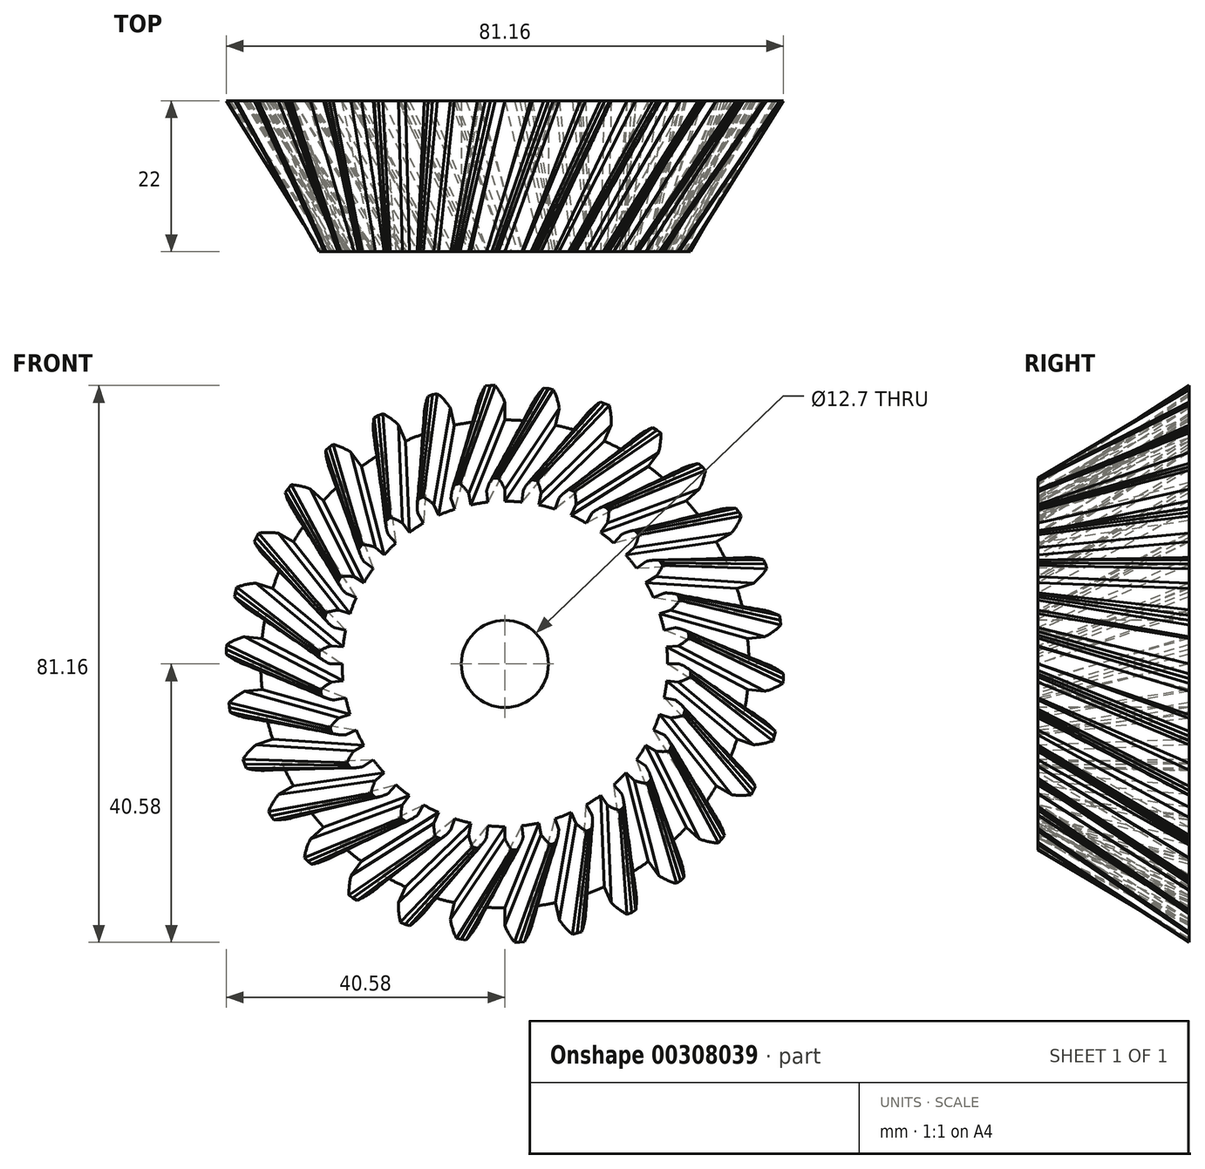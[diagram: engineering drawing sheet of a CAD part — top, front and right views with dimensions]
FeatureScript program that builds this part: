
annotation { "Feature Type Name" : "Feature", "Feature Type Description" : "" }
export const myFeature = defineFeature(function(context is Context, id is Id, definition is map)
    precondition{}
    {
        {
            var Q0;
            Q0=qCreatedBy(makeId("Front.planeOp"),FACE);
            var sketch = newSketch(context, id + "F0", { "sketchPlane" : qUnion([Q0])});
            skArc(sketch, "E0", {"start": v(-3.72, 35.37) * mm, "mid": v(-5.56, 35.12) * mm, "end": v(-7.4, 34.78) * mm});
            skLineSegment(sketch, "E1", {"start": v(0, 38.1) * mm, "end": v(0, 35.56) * mm});
            skLineSegment(sketch, "E2", {"start": v(-1.42, 40.58) * mm, "end": v(-2.13, 40.58) * mm});
            skArc(sketch, "E3.trimOffspring", {"start": v(0, 38.1) * mm, "mid": v(-0.63, 39.41) * mm, "end": v(-1.45, 40.61) * mm});
            skLineSegment(sketch, "E4.MirrorCS", {"start": v(-2.83, 40.5) * mm, "end": v(-2.13, 40.58) * mm});
            skArc(sketch, "E5.MirrorCS", {"start": v(-3.98, 37.9) * mm, "mid": v(-3.5, 39.26) * mm, "end": v(-2.8, 40.54) * mm});
            skLineSegment(sketch, "E6.MirrorCS", {"start": v(-3.98, 37.9) * mm, "end": v(-3.72, 35.37) * mm});
            skLineSegment(sketch, "E7.1.0", {"start": v(-11.77, 36.24) * mm, "end": v(-10.99, 33.82) * mm});
            skArc(sketch, "E7.1.1", {"start": v(-11.77, 36.24) * mm, "mid": v(-11.58, 37.68) * mm, "end": v(-11.18, 39.07) * mm});
            skLineSegment(sketch, "E7.1.2", {"start": v(-11.2, 39.04) * mm, "end": v(-10.52, 39.25) * mm});
            skLineSegment(sketch, "E7.1.3", {"start": v(-9.83, 39.4) * mm, "end": v(-10.52, 39.25) * mm});
            skArc(sketch, "E7.1.4", {"start": v(-7.92, 37.27) * mm, "mid": v(-8.8, 38.42) * mm, "end": v(-9.86, 39.43) * mm});
            skLineSegment(sketch, "E7.1.5", {"start": v(-7.92, 37.27) * mm, "end": v(-7.4, 34.78) * mm});
            skLineSegment(sketch, "E7.2.0", {"start": v(-19.05, 33) * mm, "end": v(-17.78, 30.8) * mm});
            skArc(sketch, "E7.2.1", {"start": v(-19.05, 33) * mm, "mid": v(-19.16, 34.45) * mm, "end": v(-19.06, 35.9) * mm});
            skLineSegment(sketch, "E7.2.2", {"start": v(-19.06, 35.86) * mm, "end": v(-18.45, 36.2) * mm});
            skLineSegment(sketch, "E7.2.3", {"start": v(-17.8, 36.5) * mm, "end": v(-18.45, 36.2) * mm});
            skArc(sketch, "E7.2.4", {"start": v(-15.5, 34.8) * mm, "mid": v(-16.6, 35.75) * mm, "end": v(-17.84, 36.52) * mm});
            skLineSegment(sketch, "E7.2.5", {"start": v(-15.5, 34.8) * mm, "end": v(-14.46, 32.49) * mm});
            skLineSegment(sketch, "E7.3.0", {"start": v(-25.5, 28.31) * mm, "end": v(-23.8, 26.43) * mm});
            skArc(sketch, "E7.3.1", {"start": v(-25.5, 28.31) * mm, "mid": v(-25.9, 29.7) * mm, "end": v(-26.1, 31.15) * mm});
            skLineSegment(sketch, "E7.3.2", {"start": v(-26.1, 31.1) * mm, "end": v(-25.57, 31.58) * mm});
            skLineSegment(sketch, "E7.3.3", {"start": v(-25, 32) * mm, "end": v(-25.57, 31.58) * mm});
            skArc(sketch, "E7.3.4", {"start": v(-22.4, 30.82) * mm, "mid": v(-23.67, 31.52) * mm, "end": v(-25.04, 32) * mm});
            skLineSegment(sketch, "E7.3.5", {"start": v(-22.4, 30.82) * mm, "end": v(-20.9, 28.77) * mm});
            skLineSegment(sketch, "E7.4.0", {"start": v(-30.82, 22.4) * mm, "end": v(-28.77, 20.9) * mm});
            skArc(sketch, "E7.4.1", {"start": v(-30.82, 22.4) * mm, "mid": v(-31.52, 23.67) * mm, "end": v(-32, 25.04) * mm});
            skLineSegment(sketch, "E7.4.2", {"start": v(-32, 25) * mm, "end": v(-31.58, 25.57) * mm});
            skLineSegment(sketch, "E7.4.3", {"start": v(-31.1, 26.1) * mm, "end": v(-31.58, 25.57) * mm});
            skArc(sketch, "E7.4.4", {"start": v(-28.31, 25.5) * mm, "mid": v(-29.7, 25.9) * mm, "end": v(-31.15, 26.1) * mm});
            skLineSegment(sketch, "E7.4.5", {"start": v(-28.31, 25.5) * mm, "end": v(-26.43, 23.8) * mm});
            skLineSegment(sketch, "E7.5.0", {"start": v(-34.8, 15.5) * mm, "end": v(-32.49, 14.46) * mm});
            skArc(sketch, "E7.5.1", {"start": v(-34.8, 15.5) * mm, "mid": v(-35.75, 16.6) * mm, "end": v(-36.52, 17.84) * mm});
            skLineSegment(sketch, "E7.5.2", {"start": v(-36.5, 17.8) * mm, "end": v(-36.2, 18.45) * mm});
            skLineSegment(sketch, "E7.5.3", {"start": v(-35.86, 19.06) * mm, "end": v(-36.2, 18.45) * mm});
            skArc(sketch, "E7.5.4", {"start": v(-33, 19.05) * mm, "mid": v(-34.45, 19.16) * mm, "end": v(-35.9, 19.06) * mm});
            skLineSegment(sketch, "E7.5.5", {"start": v(-33, 19.05) * mm, "end": v(-30.8, 17.78) * mm});
            skLineSegment(sketch, "E7.6.0", {"start": v(-37.27, 7.92) * mm, "end": v(-34.78, 7.4) * mm});
            skArc(sketch, "E7.6.1", {"start": v(-37.27, 7.92) * mm, "mid": v(-38.42, 8.8) * mm, "end": v(-39.43, 9.86) * mm});
            skLineSegment(sketch, "E7.6.2", {"start": v(-39.4, 9.83) * mm, "end": v(-39.25, 10.52) * mm});
            skLineSegment(sketch, "E7.6.3", {"start": v(-39.04, 11.2) * mm, "end": v(-39.25, 10.52) * mm});
            skArc(sketch, "E7.6.4", {"start": v(-36.24, 11.77) * mm, "mid": v(-37.68, 11.58) * mm, "end": v(-39.07, 11.18) * mm});
            skLineSegment(sketch, "E7.6.5", {"start": v(-36.24, 11.77) * mm, "end": v(-33.82, 10.99) * mm});
            skLineSegment(sketch, "E7.7.0", {"start": v(-38.1, 0) * mm, "end": v(-35.56, 0) * mm});
            skArc(sketch, "E7.7.1", {"start": v(-38.1, 0) * mm, "mid": v(-39.41, 0.63) * mm, "end": v(-40.61, 1.45) * mm});
            skLineSegment(sketch, "E7.7.2", {"start": v(-40.58, 1.42) * mm, "end": v(-40.58, 2.13) * mm});
            skLineSegment(sketch, "E7.7.3", {"start": v(-40.5, 2.83) * mm, "end": v(-40.58, 2.13) * mm});
            skArc(sketch, "E7.7.4", {"start": v(-37.9, 3.98) * mm, "mid": v(-39.26, 3.5) * mm, "end": v(-40.54, 2.8) * mm});
            skLineSegment(sketch, "E7.7.5", {"start": v(-37.9, 3.98) * mm, "end": v(-35.37, 3.72) * mm});
            skLineSegment(sketch, "E7.8.0", {"start": v(-37.27, -7.92) * mm, "end": v(-34.78, -7.4) * mm});
            skArc(sketch, "E7.8.1", {"start": v(-37.27, -7.92) * mm, "mid": v(-38.68, -7.58) * mm, "end": v(-40.03, -7.03) * mm});
            skLineSegment(sketch, "E7.8.2", {"start": v(-40, -7.05) * mm, "end": v(-40.14, -6.36) * mm});
            skLineSegment(sketch, "E7.8.3", {"start": v(-40.21, -5.65) * mm, "end": v(-40.14, -6.36) * mm});
            skArc(sketch, "E7.8.4", {"start": v(-37.9, -3.98) * mm, "mid": v(-39.13, -4.74) * mm, "end": v(-40.24, -5.68) * mm});
            skLineSegment(sketch, "E7.8.5", {"start": v(-37.9, -3.98) * mm, "end": v(-35.37, -3.72) * mm});
            skLineSegment(sketch, "E7.9.0", {"start": v(-34.8, -15.5) * mm, "end": v(-32.49, -14.46) * mm});
            skArc(sketch, "E7.9.1", {"start": v(-34.8, -15.5) * mm, "mid": v(-36.26, -15.46) * mm, "end": v(-37.7, -15.2) * mm});
            skLineSegment(sketch, "E7.9.2", {"start": v(-37.65, -15.2) * mm, "end": v(-37.94, -14.56) * mm});
            skLineSegment(sketch, "E7.9.3", {"start": v(-38.16, -13.9) * mm, "end": v(-37.94, -14.56) * mm});
            skArc(sketch, "E7.9.4", {"start": v(-36.24, -11.77) * mm, "mid": v(-37.29, -12.77) * mm, "end": v(-38.18, -13.92) * mm});
            skLineSegment(sketch, "E7.9.5", {"start": v(-36.24, -11.77) * mm, "end": v(-33.82, -10.99) * mm});
            skLineSegment(sketch, "E7.10.0", {"start": v(-30.82, -22.4) * mm, "end": v(-28.77, -20.9) * mm});
            skArc(sketch, "E7.10.1", {"start": v(-30.82, -22.4) * mm, "mid": v(-32.25, -22.66) * mm, "end": v(-33.7, -22.7) * mm});
            skLineSegment(sketch, "E7.10.2", {"start": v(-33.67, -22.7) * mm, "end": v(-34.08, -22.13) * mm});
            skLineSegment(sketch, "E7.10.3", {"start": v(-34.44, -21.52) * mm, "end": v(-34.08, -22.13) * mm});
            skArc(sketch, "E7.10.4", {"start": v(-33, -19.05) * mm, "mid": v(-33.82, -20.25) * mm, "end": v(-34.45, -21.56) * mm});
            skLineSegment(sketch, "E7.10.5", {"start": v(-33, -19.05) * mm, "end": v(-30.8, -17.78) * mm});
            skLineSegment(sketch, "E7.11.0", {"start": v(-25.5, -28.31) * mm, "end": v(-23.8, -26.43) * mm});
            skArc(sketch, "E7.11.1", {"start": v(-25.5, -28.31) * mm, "mid": v(-26.84, -28.87) * mm, "end": v(-28.25, -29.22) * mm});
            skLineSegment(sketch, "E7.11.2", {"start": v(-28.21, -29.2) * mm, "end": v(-28.74, -28.74) * mm});
            skLineSegment(sketch, "E7.11.3", {"start": v(-29.2, -28.21) * mm, "end": v(-28.74, -28.74) * mm});
            skArc(sketch, "E7.11.4", {"start": v(-28.31, -25.5) * mm, "mid": v(-28.87, -26.84) * mm, "end": v(-29.22, -28.25) * mm});
            skLineSegment(sketch, "E7.11.5", {"start": v(-28.31, -25.5) * mm, "end": v(-26.43, -23.8) * mm});
            skLineSegment(sketch, "E7.12.0", {"start": v(-19.05, -33) * mm, "end": v(-17.78, -30.8) * mm});
            skArc(sketch, "E7.12.1", {"start": v(-19.05, -33) * mm, "mid": v(-20.25, -33.82) * mm, "end": v(-21.56, -34.45) * mm});
            skLineSegment(sketch, "E7.12.2", {"start": v(-21.52, -34.44) * mm, "end": v(-22.13, -34.08) * mm});
            skLineSegment(sketch, "E7.12.3", {"start": v(-22.7, -33.67) * mm, "end": v(-22.13, -34.08) * mm});
            skArc(sketch, "E7.12.4", {"start": v(-22.4, -30.82) * mm, "mid": v(-22.66, -32.25) * mm, "end": v(-22.7, -33.7) * mm});
            skLineSegment(sketch, "E7.12.5", {"start": v(-22.4, -30.82) * mm, "end": v(-20.9, -28.77) * mm});
            skLineSegment(sketch, "E7.13.0", {"start": v(-11.77, -36.24) * mm, "end": v(-10.99, -33.82) * mm});
            skArc(sketch, "E7.13.1", {"start": v(-11.77, -36.24) * mm, "mid": v(-12.77, -37.29) * mm, "end": v(-13.92, -38.18) * mm});
            skLineSegment(sketch, "E7.13.2", {"start": v(-13.9, -38.16) * mm, "end": v(-14.56, -37.94) * mm});
            skLineSegment(sketch, "E7.13.3", {"start": v(-15.2, -37.65) * mm, "end": v(-14.56, -37.94) * mm});
            skArc(sketch, "E7.13.4", {"start": v(-15.5, -34.8) * mm, "mid": v(-15.46, -36.26) * mm, "end": v(-15.2, -37.7) * mm});
            skLineSegment(sketch, "E7.13.5", {"start": v(-15.5, -34.8) * mm, "end": v(-14.46, -32.49) * mm});
            skLineSegment(sketch, "E7.14.0", {"start": v(-3.98, -37.9) * mm, "end": v(-3.72, -35.37) * mm});
            skArc(sketch, "E7.14.1", {"start": v(-3.98, -37.9) * mm, "mid": v(-4.74, -39.13) * mm, "end": v(-5.68, -40.24) * mm});
            skLineSegment(sketch, "E7.14.2", {"start": v(-5.65, -40.21) * mm, "end": v(-6.36, -40.14) * mm});
            skLineSegment(sketch, "E7.14.3", {"start": v(-7.05, -40) * mm, "end": v(-6.36, -40.14) * mm});
            skArc(sketch, "E7.14.4", {"start": v(-7.92, -37.27) * mm, "mid": v(-7.58, -38.68) * mm, "end": v(-7.03, -40.03) * mm});
            skLineSegment(sketch, "E7.14.5", {"start": v(-7.92, -37.27) * mm, "end": v(-7.4, -34.78) * mm});
            skLineSegment(sketch, "E7.15.0", {"start": v(3.98, -37.9) * mm, "end": v(3.72, -35.37) * mm});
            skArc(sketch, "E7.15.1", {"start": v(3.98, -37.9) * mm, "mid": v(3.5, -39.26) * mm, "end": v(2.8, -40.54) * mm});
            skLineSegment(sketch, "E7.15.2", {"start": v(2.83, -40.5) * mm, "end": v(2.13, -40.58) * mm});
            skLineSegment(sketch, "E7.15.3", {"start": v(1.42, -40.58) * mm, "end": v(2.13, -40.58) * mm});
            skArc(sketch, "E7.15.4", {"start": v(0, -38.1) * mm, "mid": v(0.63, -39.41) * mm, "end": v(1.45, -40.61) * mm});
            skLineSegment(sketch, "E7.15.5", {"start": v(0, -38.1) * mm, "end": v(0, -35.56) * mm});
            skLineSegment(sketch, "E7.16.0", {"start": v(11.77, -36.24) * mm, "end": v(10.99, -33.82) * mm});
            skArc(sketch, "E7.16.1", {"start": v(11.77, -36.24) * mm, "mid": v(11.58, -37.68) * mm, "end": v(11.18, -39.07) * mm});
            skLineSegment(sketch, "E7.16.2", {"start": v(11.2, -39.04) * mm, "end": v(10.52, -39.25) * mm});
            skLineSegment(sketch, "E7.16.3", {"start": v(9.83, -39.4) * mm, "end": v(10.52, -39.25) * mm});
            skArc(sketch, "E7.16.4", {"start": v(7.92, -37.27) * mm, "mid": v(8.8, -38.42) * mm, "end": v(9.86, -39.43) * mm});
            skLineSegment(sketch, "E7.16.5", {"start": v(7.92, -37.27) * mm, "end": v(7.4, -34.78) * mm});
            skLineSegment(sketch, "E7.17.0", {"start": v(19.05, -33) * mm, "end": v(17.78, -30.8) * mm});
            skArc(sketch, "E7.17.1", {"start": v(19.05, -33) * mm, "mid": v(19.16, -34.45) * mm, "end": v(19.06, -35.9) * mm});
            skLineSegment(sketch, "E7.17.2", {"start": v(19.06, -35.86) * mm, "end": v(18.45, -36.2) * mm});
            skLineSegment(sketch, "E7.17.3", {"start": v(17.8, -36.5) * mm, "end": v(18.45, -36.2) * mm});
            skArc(sketch, "E7.17.4", {"start": v(15.5, -34.8) * mm, "mid": v(16.6, -35.75) * mm, "end": v(17.84, -36.52) * mm});
            skLineSegment(sketch, "E7.17.5", {"start": v(15.5, -34.8) * mm, "end": v(14.46, -32.49) * mm});
            skLineSegment(sketch, "E7.18.0", {"start": v(25.5, -28.31) * mm, "end": v(23.8, -26.43) * mm});
            skArc(sketch, "E7.18.1", {"start": v(25.5, -28.31) * mm, "mid": v(25.9, -29.7) * mm, "end": v(26.1, -31.15) * mm});
            skLineSegment(sketch, "E7.18.2", {"start": v(26.1, -31.1) * mm, "end": v(25.57, -31.58) * mm});
            skLineSegment(sketch, "E7.18.3", {"start": v(25, -32) * mm, "end": v(25.57, -31.58) * mm});
            skArc(sketch, "E7.18.4", {"start": v(22.4, -30.82) * mm, "mid": v(23.67, -31.52) * mm, "end": v(25.04, -32) * mm});
            skLineSegment(sketch, "E7.18.5", {"start": v(22.4, -30.82) * mm, "end": v(20.9, -28.77) * mm});
            skLineSegment(sketch, "E7.19.0", {"start": v(30.82, -22.4) * mm, "end": v(28.77, -20.9) * mm});
            skArc(sketch, "E7.19.1", {"start": v(30.82, -22.4) * mm, "mid": v(31.52, -23.67) * mm, "end": v(32, -25.04) * mm});
            skLineSegment(sketch, "E7.19.2", {"start": v(32, -25) * mm, "end": v(31.58, -25.57) * mm});
            skLineSegment(sketch, "E7.19.3", {"start": v(31.1, -26.1) * mm, "end": v(31.58, -25.57) * mm});
            skArc(sketch, "E7.19.4", {"start": v(28.31, -25.5) * mm, "mid": v(29.7, -25.9) * mm, "end": v(31.15, -26.1) * mm});
            skLineSegment(sketch, "E7.19.5", {"start": v(28.31, -25.5) * mm, "end": v(26.43, -23.8) * mm});
            skLineSegment(sketch, "E7.20.0", {"start": v(34.8, -15.5) * mm, "end": v(32.49, -14.46) * mm});
            skArc(sketch, "E7.20.1", {"start": v(34.8, -15.5) * mm, "mid": v(35.75, -16.6) * mm, "end": v(36.52, -17.84) * mm});
            skLineSegment(sketch, "E7.20.2", {"start": v(36.5, -17.8) * mm, "end": v(36.2, -18.45) * mm});
            skLineSegment(sketch, "E7.20.3", {"start": v(35.86, -19.06) * mm, "end": v(36.2, -18.45) * mm});
            skArc(sketch, "E7.20.4", {"start": v(33, -19.05) * mm, "mid": v(34.45, -19.16) * mm, "end": v(35.9, -19.06) * mm});
            skLineSegment(sketch, "E7.20.5", {"start": v(33, -19.05) * mm, "end": v(30.8, -17.78) * mm});
            skLineSegment(sketch, "E7.21.0", {"start": v(37.27, -7.92) * mm, "end": v(34.78, -7.4) * mm});
            skArc(sketch, "E7.21.1", {"start": v(37.27, -7.92) * mm, "mid": v(38.42, -8.8) * mm, "end": v(39.43, -9.86) * mm});
            skLineSegment(sketch, "E7.21.2", {"start": v(39.4, -9.83) * mm, "end": v(39.25, -10.52) * mm});
            skLineSegment(sketch, "E7.21.3", {"start": v(39.04, -11.2) * mm, "end": v(39.25, -10.52) * mm});
            skArc(sketch, "E7.21.4", {"start": v(36.24, -11.77) * mm, "mid": v(37.68, -11.58) * mm, "end": v(39.07, -11.18) * mm});
            skLineSegment(sketch, "E7.21.5", {"start": v(36.24, -11.77) * mm, "end": v(33.82, -10.99) * mm});
            skLineSegment(sketch, "E7.22.0", {"start": v(38.1, 0) * mm, "end": v(35.56, 0) * mm});
            skArc(sketch, "E7.22.1", {"start": v(38.1, 0) * mm, "mid": v(39.41, -0.63) * mm, "end": v(40.61, -1.45) * mm});
            skLineSegment(sketch, "E7.22.2", {"start": v(40.58, -1.42) * mm, "end": v(40.58, -2.13) * mm});
            skLineSegment(sketch, "E7.22.3", {"start": v(40.5, -2.83) * mm, "end": v(40.58, -2.13) * mm});
            skArc(sketch, "E7.22.4", {"start": v(37.9, -3.98) * mm, "mid": v(39.26, -3.5) * mm, "end": v(40.54, -2.8) * mm});
            skLineSegment(sketch, "E7.22.5", {"start": v(37.9, -3.98) * mm, "end": v(35.37, -3.72) * mm});
            skLineSegment(sketch, "E7.23.0", {"start": v(37.27, 7.92) * mm, "end": v(34.78, 7.4) * mm});
            skArc(sketch, "E7.23.1", {"start": v(37.27, 7.92) * mm, "mid": v(38.68, 7.58) * mm, "end": v(40.03, 7.03) * mm});
            skLineSegment(sketch, "E7.23.2", {"start": v(40, 7.05) * mm, "end": v(40.14, 6.36) * mm});
            skLineSegment(sketch, "E7.23.3", {"start": v(40.21, 5.65) * mm, "end": v(40.14, 6.36) * mm});
            skArc(sketch, "E7.23.4", {"start": v(37.9, 3.98) * mm, "mid": v(39.13, 4.74) * mm, "end": v(40.24, 5.68) * mm});
            skLineSegment(sketch, "E7.23.5", {"start": v(37.9, 3.98) * mm, "end": v(35.37, 3.72) * mm});
            skLineSegment(sketch, "E7.24.0", {"start": v(34.8, 15.5) * mm, "end": v(32.49, 14.46) * mm});
            skArc(sketch, "E7.24.1", {"start": v(34.8, 15.5) * mm, "mid": v(36.26, 15.46) * mm, "end": v(37.7, 15.2) * mm});
            skLineSegment(sketch, "E7.24.2", {"start": v(37.65, 15.2) * mm, "end": v(37.94, 14.56) * mm});
            skLineSegment(sketch, "E7.24.3", {"start": v(38.16, 13.9) * mm, "end": v(37.94, 14.56) * mm});
            skArc(sketch, "E7.24.4", {"start": v(36.24, 11.77) * mm, "mid": v(37.29, 12.77) * mm, "end": v(38.18, 13.92) * mm});
            skLineSegment(sketch, "E7.24.5", {"start": v(36.24, 11.77) * mm, "end": v(33.82, 10.99) * mm});
            skLineSegment(sketch, "E7.25.0", {"start": v(30.82, 22.4) * mm, "end": v(28.77, 20.9) * mm});
            skArc(sketch, "E7.25.1", {"start": v(30.82, 22.4) * mm, "mid": v(32.25, 22.66) * mm, "end": v(33.7, 22.7) * mm});
            skLineSegment(sketch, "E7.25.2", {"start": v(33.67, 22.7) * mm, "end": v(34.08, 22.13) * mm});
            skLineSegment(sketch, "E7.25.3", {"start": v(34.44, 21.52) * mm, "end": v(34.08, 22.13) * mm});
            skArc(sketch, "E7.25.4", {"start": v(33, 19.05) * mm, "mid": v(33.82, 20.25) * mm, "end": v(34.45, 21.56) * mm});
            skLineSegment(sketch, "E7.25.5", {"start": v(33, 19.05) * mm, "end": v(30.8, 17.78) * mm});
            skLineSegment(sketch, "E7.26.0", {"start": v(25.5, 28.31) * mm, "end": v(23.8, 26.43) * mm});
            skArc(sketch, "E7.26.1", {"start": v(25.5, 28.31) * mm, "mid": v(26.84, 28.87) * mm, "end": v(28.25, 29.22) * mm});
            skLineSegment(sketch, "E7.26.2", {"start": v(28.21, 29.2) * mm, "end": v(28.74, 28.74) * mm});
            skLineSegment(sketch, "E7.26.3", {"start": v(29.2, 28.21) * mm, "end": v(28.74, 28.74) * mm});
            skArc(sketch, "E7.26.4", {"start": v(28.31, 25.5) * mm, "mid": v(28.87, 26.84) * mm, "end": v(29.22, 28.25) * mm});
            skLineSegment(sketch, "E7.26.5", {"start": v(28.31, 25.5) * mm, "end": v(26.43, 23.8) * mm});
            skLineSegment(sketch, "E7.27.0", {"start": v(19.05, 33) * mm, "end": v(17.78, 30.8) * mm});
            skArc(sketch, "E7.27.1", {"start": v(19.05, 33) * mm, "mid": v(20.25, 33.82) * mm, "end": v(21.56, 34.45) * mm});
            skLineSegment(sketch, "E7.27.2", {"start": v(21.52, 34.44) * mm, "end": v(22.13, 34.08) * mm});
            skLineSegment(sketch, "E7.27.3", {"start": v(22.7, 33.67) * mm, "end": v(22.13, 34.08) * mm});
            skArc(sketch, "E7.27.4", {"start": v(22.4, 30.82) * mm, "mid": v(22.66, 32.25) * mm, "end": v(22.7, 33.7) * mm});
            skLineSegment(sketch, "E7.27.5", {"start": v(22.4, 30.82) * mm, "end": v(20.9, 28.77) * mm});
            skLineSegment(sketch, "E7.28.0", {"start": v(11.77, 36.24) * mm, "end": v(10.99, 33.82) * mm});
            skArc(sketch, "E7.28.1", {"start": v(11.77, 36.24) * mm, "mid": v(12.77, 37.29) * mm, "end": v(13.92, 38.18) * mm});
            skLineSegment(sketch, "E7.28.2", {"start": v(13.9, 38.16) * mm, "end": v(14.56, 37.94) * mm});
            skLineSegment(sketch, "E7.28.3", {"start": v(15.2, 37.65) * mm, "end": v(14.56, 37.94) * mm});
            skArc(sketch, "E7.28.4", {"start": v(15.5, 34.8) * mm, "mid": v(15.46, 36.26) * mm, "end": v(15.2, 37.7) * mm});
            skLineSegment(sketch, "E7.28.5", {"start": v(15.5, 34.8) * mm, "end": v(14.46, 32.49) * mm});
            skLineSegment(sketch, "E7.29.0", {"start": v(3.98, 37.9) * mm, "end": v(3.72, 35.37) * mm});
            skArc(sketch, "E7.29.1", {"start": v(3.98, 37.9) * mm, "mid": v(4.74, 39.13) * mm, "end": v(5.68, 40.24) * mm});
            skLineSegment(sketch, "E7.29.2", {"start": v(5.65, 40.21) * mm, "end": v(6.36, 40.14) * mm});
            skLineSegment(sketch, "E7.29.3", {"start": v(7.05, 40) * mm, "end": v(6.36, 40.14) * mm});
            skArc(sketch, "E7.29.4", {"start": v(7.92, 37.27) * mm, "mid": v(7.58, 38.68) * mm, "end": v(7.03, 40.03) * mm});
            skLineSegment(sketch, "E7.29.5", {"start": v(7.92, 37.27) * mm, "end": v(7.4, 34.78) * mm});
            skArc(sketch, "E8.trimOffspring", {"start": v(-10.99, 33.82) * mm, "mid": v(-12.74, 33.2) * mm, "end": v(-14.46, 32.49) * mm});
            skArc(sketch, "E9.trimOffspring", {"start": v(3.72, 35.37) * mm, "mid": v(1.86, 35.51) * mm, "end": v(0, 35.56) * mm});
            skArc(sketch, "E10.trimOffspring", {"start": v(10.99, 33.82) * mm, "mid": v(9.2, 34.35) * mm, "end": v(7.4, 34.78) * mm});
            skArc(sketch, "E11.trimOffspring", {"start": v(-17.78, 30.8) * mm, "mid": v(-19.37, 29.82) * mm, "end": v(-20.9, 28.77) * mm});
            skArc(sketch, "E12.trimOffspring", {"start": v(-23.8, 26.43) * mm, "mid": v(-25.14, 25.14) * mm, "end": v(-26.43, 23.8) * mm});
            skArc(sketch, "E13.trimOffspring", {"start": v(17.78, 30.8) * mm, "mid": v(16.14, 31.68) * mm, "end": v(14.46, 32.49) * mm});
            skArc(sketch, "E14.trimOffspring", {"start": v(23.8, 26.43) * mm, "mid": v(22.38, 27.64) * mm, "end": v(20.9, 28.77) * mm});
            skArc(sketch, "E15.trimOffspring", {"start": v(-32.49, 14.46) * mm, "mid": v(-33.2, 12.74) * mm, "end": v(-33.82, 10.99) * mm});
            skArc(sketch, "E16.trimOffspring", {"start": v(-34.78, 7.4) * mm, "mid": v(-35.12, 5.56) * mm, "end": v(-35.37, 3.72) * mm});
            skArc(sketch, "E17.trimOffspring", {"start": v(-28.77, 20.9) * mm, "mid": v(-29.82, 19.37) * mm, "end": v(-30.8, 17.78) * mm});
            skArc(sketch, "E18.trimOffspring", {"start": v(28.77, 20.9) * mm, "mid": v(27.64, 22.38) * mm, "end": v(26.43, 23.8) * mm});
            skArc(sketch, "E19.trimOffspring", {"start": v(32.49, 14.46) * mm, "mid": v(31.68, 16.14) * mm, "end": v(30.8, 17.78) * mm});
            skArc(sketch, "E20.trimOffspring", {"start": v(-35.56, 0) * mm, "mid": v(-35.51, -1.86) * mm, "end": v(-35.37, -3.72) * mm});
            skArc(sketch, "E21.trimOffspring", {"start": v(34.78, 7.4) * mm, "mid": v(34.35, 9.2) * mm, "end": v(33.82, 10.99) * mm});
            skArc(sketch, "E22.trimOffspring", {"start": v(-34.78, -7.4) * mm, "mid": v(-34.35, -9.2) * mm, "end": v(-33.82, -10.99) * mm});
            skArc(sketch, "E23.trimOffspring", {"start": v(35.56, 0) * mm, "mid": v(35.51, 1.86) * mm, "end": v(35.37, 3.72) * mm});
            skArc(sketch, "E24.trimOffspring", {"start": v(-32.49, -14.46) * mm, "mid": v(-31.68, -16.14) * mm, "end": v(-30.8, -17.78) * mm});
            skArc(sketch, "E25.trimOffspring", {"start": v(34.78, -7.4) * mm, "mid": v(35.12, -5.56) * mm, "end": v(35.37, -3.72) * mm});
            skArc(sketch, "E26.trimOffspring", {"start": v(-28.77, -20.9) * mm, "mid": v(-27.64, -22.38) * mm, "end": v(-26.43, -23.8) * mm});
            skArc(sketch, "E27.trimOffspring", {"start": v(32.49, -14.46) * mm, "mid": v(33.2, -12.74) * mm, "end": v(33.82, -10.99) * mm});
            skArc(sketch, "E28.trimOffspring", {"start": v(-23.8, -26.43) * mm, "mid": v(-22.38, -27.64) * mm, "end": v(-20.9, -28.77) * mm});
            skArc(sketch, "E29.trimOffspring", {"start": v(28.77, -20.9) * mm, "mid": v(29.82, -19.37) * mm, "end": v(30.8, -17.78) * mm});
            skArc(sketch, "E30.trimOffspring", {"start": v(-17.78, -30.8) * mm, "mid": v(-16.14, -31.68) * mm, "end": v(-14.46, -32.49) * mm});
            skArc(sketch, "E31.trimOffspring", {"start": v(23.8, -26.43) * mm, "mid": v(25.14, -25.14) * mm, "end": v(26.43, -23.8) * mm});
            skArc(sketch, "E32.trimOffspring", {"start": v(-10.99, -33.82) * mm, "mid": v(-9.2, -34.35) * mm, "end": v(-7.4, -34.78) * mm});
            skArc(sketch, "E33.trimOffspring", {"start": v(17.78, -30.8) * mm, "mid": v(19.37, -29.82) * mm, "end": v(20.9, -28.77) * mm});
            skArc(sketch, "E34.trimOffspring", {"start": v(-3.72, -35.37) * mm, "mid": v(-1.86, -35.51) * mm, "end": v(0, -35.56) * mm});
            skArc(sketch, "E35.trimOffspring", {"start": v(10.99, -33.82) * mm, "mid": v(12.74, -33.2) * mm, "end": v(14.46, -32.49) * mm});
            skArc(sketch, "E36.trimOffspring", {"start": v(3.72, -35.37) * mm, "mid": v(5.56, -35.12) * mm, "end": v(7.4, -34.78) * mm});
            skSolve(sketch);
        }
        {
            var Q0;
            Q0=makeQuery(id+"F0.imprint","IMPRINT",FACE,{"disambiguationData":[TD([[makeQuery(id+"F0.imprint","IMPRINT",EDGE,{"derivedFrom":sQuery(id+"F0.wireOp",EDGE,"E0")}),1.0]])]});
            cPlane(context, id + "F1", {"entities" : qUnion([Q0]), "cplaneType" : CPlaneType.OFFSET, "offset" : 22 * mm, "width" : 152.4 * mm, "height" : 152.4 * mm});
        }
        {
            var Q0;
            Q0=qCreatedBy(id+"F1.planeOp",FACE);
            var sketch = newSketch(context, id + "F2", { "sketchPlane" : qUnion([Q0])});
            skArc(sketch, "E37", {"start": v(-2.48, 23.58) * mm, "mid": v(-3.7, 23.42) * mm, "end": v(-4.93, 23.2) * mm});
            skArc(sketch, "E38.trimOffspring", {"start": v(0, 25.4) * mm, "mid": v(-0.41, 26.27) * mm, "end": v(-0.96, 27.07) * mm});
            skLineSegment(sketch, "E39", {"start": v(-0.96, 27.07) * mm, "end": v(-1.42, 27.07) * mm});
            skLineSegment(sketch, "E40", {"start": v(0, 25.4) * mm, "end": v(0, 23.71) * mm});
            skLineSegment(sketch, "E41.MirrorCS", {"start": v(-1.88, 27.02) * mm, "end": v(-1.42, 27.07) * mm});
            skArc(sketch, "E42.MirrorCS", {"start": v(-2.66, 25.26) * mm, "mid": v(-2.33, 26.17) * mm, "end": v(-1.88, 27.02) * mm});
            skLineSegment(sketch, "E43.MirrorCS", {"start": v(-2.66, 25.26) * mm, "end": v(-2.48, 23.58) * mm});
            skLineSegment(sketch, "E44.1.0", {"start": v(-7.85, 24.16) * mm, "end": v(-7.33, 22.55) * mm});
            skArc(sketch, "E44.1.1", {"start": v(-7.85, 24.16) * mm, "mid": v(-7.72, 25.11) * mm, "end": v(-7.46, 26.04) * mm});
            skLineSegment(sketch, "E44.1.2", {"start": v(-7.46, 26.04) * mm, "end": v(-7.02, 26.19) * mm});
            skLineSegment(sketch, "E44.1.3", {"start": v(-6.56, 26.28) * mm, "end": v(-7.02, 26.19) * mm});
            skArc(sketch, "E44.1.4", {"start": v(-5.28, 24.84) * mm, "mid": v(-5.87, 25.61) * mm, "end": v(-6.56, 26.28) * mm});
            skLineSegment(sketch, "E44.1.5", {"start": v(-5.28, 24.84) * mm, "end": v(-4.93, 23.2) * mm});
            skLineSegment(sketch, "E44.2.0", {"start": v(-12.7, 22) * mm, "end": v(-11.86, 20.53) * mm});
            skArc(sketch, "E44.2.1", {"start": v(-12.7, 22) * mm, "mid": v(-12.78, 22.96) * mm, "end": v(-12.7, 23.92) * mm});
            skLineSegment(sketch, "E44.2.2", {"start": v(-12.7, 23.92) * mm, "end": v(-12.3, 24.15) * mm});
            skLineSegment(sketch, "E44.2.3", {"start": v(-11.88, 24.34) * mm, "end": v(-12.3, 24.15) * mm});
            skArc(sketch, "E44.2.4", {"start": v(-10.33, 23.2) * mm, "mid": v(-11.06, 23.83) * mm, "end": v(-11.88, 24.34) * mm});
            skLineSegment(sketch, "E44.2.5", {"start": v(-10.33, 23.2) * mm, "end": v(-9.64, 21.66) * mm});
            skLineSegment(sketch, "E44.3.0", {"start": v(-17, 18.88) * mm, "end": v(-15.87, 17.62) * mm});
            skArc(sketch, "E44.3.1", {"start": v(-17, 18.88) * mm, "mid": v(-17.27, 19.8) * mm, "end": v(-17.4, 20.76) * mm});
            skLineSegment(sketch, "E44.3.2", {"start": v(-17.4, 20.76) * mm, "end": v(-17.06, 21.07) * mm});
            skLineSegment(sketch, "E44.3.3", {"start": v(-16.69, 21.34) * mm, "end": v(-17.06, 21.07) * mm});
            skArc(sketch, "E44.3.4", {"start": v(-14.93, 20.55) * mm, "mid": v(-15.78, 21.01) * mm, "end": v(-16.69, 21.34) * mm});
            skLineSegment(sketch, "E44.3.5", {"start": v(-14.93, 20.55) * mm, "end": v(-13.94, 19.18) * mm});
            skLineSegment(sketch, "E44.4.0", {"start": v(-20.55, 14.93) * mm, "end": v(-19.18, 13.94) * mm});
            skArc(sketch, "E44.4.1", {"start": v(-20.55, 14.93) * mm, "mid": v(-21.01, 15.78) * mm, "end": v(-21.34, 16.69) * mm});
            skLineSegment(sketch, "E44.4.2", {"start": v(-21.34, 16.69) * mm, "end": v(-21.07, 17.06) * mm});
            skLineSegment(sketch, "E44.4.3", {"start": v(-20.76, 17.4) * mm, "end": v(-21.07, 17.06) * mm});
            skArc(sketch, "E44.4.4", {"start": v(-18.88, 17) * mm, "mid": v(-19.8, 17.27) * mm, "end": v(-20.76, 17.4) * mm});
            skLineSegment(sketch, "E44.4.5", {"start": v(-18.88, 17) * mm, "end": v(-17.62, 15.87) * mm});
            skLineSegment(sketch, "E44.5.0", {"start": v(-23.2, 10.33) * mm, "end": v(-21.66, 9.64) * mm});
            skArc(sketch, "E44.5.1", {"start": v(-23.2, 10.33) * mm, "mid": v(-23.83, 11.06) * mm, "end": v(-24.34, 11.88) * mm});
            skLineSegment(sketch, "E44.5.2", {"start": v(-24.34, 11.88) * mm, "end": v(-24.15, 12.3) * mm});
            skLineSegment(sketch, "E44.5.3", {"start": v(-23.92, 12.7) * mm, "end": v(-24.15, 12.3) * mm});
            skArc(sketch, "E44.5.4", {"start": v(-22, 12.7) * mm, "mid": v(-22.96, 12.78) * mm, "end": v(-23.92, 12.7) * mm});
            skLineSegment(sketch, "E44.5.5", {"start": v(-22, 12.7) * mm, "end": v(-20.53, 11.86) * mm});
            skLineSegment(sketch, "E44.6.0", {"start": v(-24.84, 5.28) * mm, "end": v(-23.2, 4.93) * mm});
            skArc(sketch, "E44.6.1", {"start": v(-24.84, 5.28) * mm, "mid": v(-25.61, 5.87) * mm, "end": v(-26.28, 6.56) * mm});
            skLineSegment(sketch, "E44.6.2", {"start": v(-26.28, 6.56) * mm, "end": v(-26.19, 7.02) * mm});
            skLineSegment(sketch, "E44.6.3", {"start": v(-26.04, 7.46) * mm, "end": v(-26.19, 7.02) * mm});
            skArc(sketch, "E44.6.4", {"start": v(-24.16, 7.85) * mm, "mid": v(-25.11, 7.72) * mm, "end": v(-26.04, 7.46) * mm});
            skLineSegment(sketch, "E44.6.5", {"start": v(-24.16, 7.85) * mm, "end": v(-22.55, 7.33) * mm});
            skLineSegment(sketch, "E44.7.0", {"start": v(-25.4, 0) * mm, "end": v(-23.71, 0) * mm});
            skArc(sketch, "E44.7.1", {"start": v(-25.4, 0) * mm, "mid": v(-26.27, 0.41) * mm, "end": v(-27.07, 0.96) * mm});
            skLineSegment(sketch, "E44.7.2", {"start": v(-27.07, 0.96) * mm, "end": v(-27.07, 1.42) * mm});
            skLineSegment(sketch, "E44.7.3", {"start": v(-27.02, 1.88) * mm, "end": v(-27.07, 1.42) * mm});
            skArc(sketch, "E44.7.4", {"start": v(-25.26, 2.66) * mm, "mid": v(-26.17, 2.33) * mm, "end": v(-27.02, 1.88) * mm});
            skLineSegment(sketch, "E44.7.5", {"start": v(-25.26, 2.66) * mm, "end": v(-23.58, 2.48) * mm});
            skLineSegment(sketch, "E44.8.0", {"start": v(-24.84, -5.28) * mm, "end": v(-23.2, -4.93) * mm});
            skArc(sketch, "E44.8.1", {"start": v(-24.84, -5.28) * mm, "mid": v(-25.78, -5.06) * mm, "end": v(-26.68, -4.7) * mm});
            skLineSegment(sketch, "E44.8.2", {"start": v(-26.68, -4.7) * mm, "end": v(-26.78, -4.24) * mm});
            skLineSegment(sketch, "E44.8.3", {"start": v(-26.82, -3.78) * mm, "end": v(-26.78, -4.24) * mm});
            skArc(sketch, "E44.8.4", {"start": v(-25.26, -2.66) * mm, "mid": v(-26.09, -3.16) * mm, "end": v(-26.82, -3.78) * mm});
            skLineSegment(sketch, "E44.8.5", {"start": v(-25.26, -2.66) * mm, "end": v(-23.58, -2.48) * mm});
            skLineSegment(sketch, "E44.9.0", {"start": v(-23.2, -10.33) * mm, "end": v(-21.66, -9.64) * mm});
            skArc(sketch, "E44.9.1", {"start": v(-23.2, -10.33) * mm, "mid": v(-24.17, -10.3) * mm, "end": v(-25.12, -10.14) * mm});
            skLineSegment(sketch, "E44.9.2", {"start": v(-25.12, -10.14) * mm, "end": v(-25.3, -9.72) * mm});
            skLineSegment(sketch, "E44.9.3", {"start": v(-25.45, -9.28) * mm, "end": v(-25.3, -9.72) * mm});
            skArc(sketch, "E44.9.4", {"start": v(-24.16, -7.85) * mm, "mid": v(-24.86, -8.51) * mm, "end": v(-25.45, -9.28) * mm});
            skLineSegment(sketch, "E44.9.5", {"start": v(-24.16, -7.85) * mm, "end": v(-22.55, -7.33) * mm});
            skLineSegment(sketch, "E44.10.0", {"start": v(-20.55, -14.93) * mm, "end": v(-19.18, -13.94) * mm});
            skArc(sketch, "E44.10.1", {"start": v(-20.55, -14.93) * mm, "mid": v(-21.5, -15.1) * mm, "end": v(-22.46, -15.14) * mm});
            skLineSegment(sketch, "E44.10.2", {"start": v(-22.46, -15.14) * mm, "end": v(-22.74, -14.76) * mm});
            skLineSegment(sketch, "E44.10.3", {"start": v(-22.97, -14.36) * mm, "end": v(-22.74, -14.76) * mm});
            skArc(sketch, "E44.10.4", {"start": v(-22, -12.7) * mm, "mid": v(-22.55, -13.5) * mm, "end": v(-22.97, -14.36) * mm});
            skLineSegment(sketch, "E44.10.5", {"start": v(-22, -12.7) * mm, "end": v(-20.53, -11.86) * mm});
            skLineSegment(sketch, "E44.11.0", {"start": v(-17, -18.88) * mm, "end": v(-15.87, -17.62) * mm});
            skArc(sketch, "E44.11.1", {"start": v(-17, -18.88) * mm, "mid": v(-17.89, -19.25) * mm, "end": v(-18.83, -19.48) * mm});
            skLineSegment(sketch, "E44.11.2", {"start": v(-18.83, -19.48) * mm, "end": v(-19.17, -19.17) * mm});
            skLineSegment(sketch, "E44.11.3", {"start": v(-19.48, -18.83) * mm, "end": v(-19.17, -19.17) * mm});
            skArc(sketch, "E44.11.4", {"start": v(-18.88, -17) * mm, "mid": v(-19.25, -17.89) * mm, "end": v(-19.48, -18.83) * mm});
            skLineSegment(sketch, "E44.11.5", {"start": v(-18.88, -17) * mm, "end": v(-17.62, -15.87) * mm});
            skLineSegment(sketch, "E44.12.0", {"start": v(-12.7, -22) * mm, "end": v(-11.86, -20.53) * mm});
            skArc(sketch, "E44.12.1", {"start": v(-12.7, -22) * mm, "mid": v(-13.5, -22.55) * mm, "end": v(-14.36, -22.97) * mm});
            skLineSegment(sketch, "E44.12.2", {"start": v(-14.36, -22.97) * mm, "end": v(-14.76, -22.74) * mm});
            skLineSegment(sketch, "E44.12.3", {"start": v(-15.14, -22.46) * mm, "end": v(-14.76, -22.74) * mm});
            skArc(sketch, "E44.12.4", {"start": v(-14.93, -20.55) * mm, "mid": v(-15.1, -21.5) * mm, "end": v(-15.14, -22.46) * mm});
            skLineSegment(sketch, "E44.12.5", {"start": v(-14.93, -20.55) * mm, "end": v(-13.94, -19.18) * mm});
            skLineSegment(sketch, "E44.13.0", {"start": v(-7.85, -24.16) * mm, "end": v(-7.33, -22.55) * mm});
            skArc(sketch, "E44.13.1", {"start": v(-7.85, -24.16) * mm, "mid": v(-8.51, -24.86) * mm, "end": v(-9.28, -25.45) * mm});
            skLineSegment(sketch, "E44.13.2", {"start": v(-9.28, -25.45) * mm, "end": v(-9.72, -25.3) * mm});
            skLineSegment(sketch, "E44.13.3", {"start": v(-10.14, -25.12) * mm, "end": v(-9.72, -25.3) * mm});
            skArc(sketch, "E44.13.4", {"start": v(-10.33, -23.2) * mm, "mid": v(-10.3, -24.17) * mm, "end": v(-10.14, -25.12) * mm});
            skLineSegment(sketch, "E44.13.5", {"start": v(-10.33, -23.2) * mm, "end": v(-9.64, -21.66) * mm});
            skLineSegment(sketch, "E44.14.0", {"start": v(-2.66, -25.26) * mm, "end": v(-2.48, -23.58) * mm});
            skArc(sketch, "E44.14.1", {"start": v(-2.66, -25.26) * mm, "mid": v(-3.16, -26.09) * mm, "end": v(-3.78, -26.82) * mm});
            skLineSegment(sketch, "E44.14.2", {"start": v(-3.78, -26.82) * mm, "end": v(-4.24, -26.78) * mm});
            skLineSegment(sketch, "E44.14.3", {"start": v(-4.7, -26.68) * mm, "end": v(-4.24, -26.78) * mm});
            skArc(sketch, "E44.14.4", {"start": v(-5.28, -24.84) * mm, "mid": v(-5.06, -25.78) * mm, "end": v(-4.7, -26.68) * mm});
            skLineSegment(sketch, "E44.14.5", {"start": v(-5.28, -24.84) * mm, "end": v(-4.93, -23.2) * mm});
            skLineSegment(sketch, "E44.15.0", {"start": v(2.66, -25.26) * mm, "end": v(2.48, -23.58) * mm});
            skArc(sketch, "E44.15.1", {"start": v(2.66, -25.26) * mm, "mid": v(2.33, -26.17) * mm, "end": v(1.88, -27.02) * mm});
            skLineSegment(sketch, "E44.15.2", {"start": v(1.88, -27.02) * mm, "end": v(1.42, -27.07) * mm});
            skLineSegment(sketch, "E44.15.3", {"start": v(0.96, -27.07) * mm, "end": v(1.42, -27.07) * mm});
            skArc(sketch, "E44.15.4", {"start": v(0, -25.4) * mm, "mid": v(0.41, -26.27) * mm, "end": v(0.96, -27.07) * mm});
            skLineSegment(sketch, "E44.15.5", {"start": v(0, -25.4) * mm, "end": v(0, -23.71) * mm});
            skLineSegment(sketch, "E44.16.0", {"start": v(7.85, -24.16) * mm, "end": v(7.33, -22.55) * mm});
            skArc(sketch, "E44.16.1", {"start": v(7.85, -24.16) * mm, "mid": v(7.72, -25.11) * mm, "end": v(7.46, -26.04) * mm});
            skLineSegment(sketch, "E44.16.2", {"start": v(7.46, -26.04) * mm, "end": v(7.02, -26.19) * mm});
            skLineSegment(sketch, "E44.16.3", {"start": v(6.56, -26.28) * mm, "end": v(7.02, -26.19) * mm});
            skArc(sketch, "E44.16.4", {"start": v(5.28, -24.84) * mm, "mid": v(5.87, -25.61) * mm, "end": v(6.56, -26.28) * mm});
            skLineSegment(sketch, "E44.16.5", {"start": v(5.28, -24.84) * mm, "end": v(4.93, -23.2) * mm});
            skLineSegment(sketch, "E44.17.0", {"start": v(12.7, -22) * mm, "end": v(11.86, -20.53) * mm});
            skArc(sketch, "E44.17.1", {"start": v(12.7, -22) * mm, "mid": v(12.78, -22.96) * mm, "end": v(12.7, -23.92) * mm});
            skLineSegment(sketch, "E44.17.2", {"start": v(12.7, -23.92) * mm, "end": v(12.3, -24.15) * mm});
            skLineSegment(sketch, "E44.17.3", {"start": v(11.88, -24.34) * mm, "end": v(12.3, -24.15) * mm});
            skArc(sketch, "E44.17.4", {"start": v(10.33, -23.2) * mm, "mid": v(11.06, -23.83) * mm, "end": v(11.88, -24.34) * mm});
            skLineSegment(sketch, "E44.17.5", {"start": v(10.33, -23.2) * mm, "end": v(9.64, -21.66) * mm});
            skLineSegment(sketch, "E44.18.0", {"start": v(17, -18.88) * mm, "end": v(15.87, -17.62) * mm});
            skArc(sketch, "E44.18.1", {"start": v(17, -18.88) * mm, "mid": v(17.27, -19.8) * mm, "end": v(17.4, -20.76) * mm});
            skLineSegment(sketch, "E44.18.2", {"start": v(17.4, -20.76) * mm, "end": v(17.06, -21.07) * mm});
            skLineSegment(sketch, "E44.18.3", {"start": v(16.69, -21.34) * mm, "end": v(17.06, -21.07) * mm});
            skArc(sketch, "E44.18.4", {"start": v(14.93, -20.55) * mm, "mid": v(15.78, -21.01) * mm, "end": v(16.69, -21.34) * mm});
            skLineSegment(sketch, "E44.18.5", {"start": v(14.93, -20.55) * mm, "end": v(13.94, -19.18) * mm});
            skLineSegment(sketch, "E44.19.0", {"start": v(20.55, -14.93) * mm, "end": v(19.18, -13.94) * mm});
            skArc(sketch, "E44.19.1", {"start": v(20.55, -14.93) * mm, "mid": v(21.01, -15.78) * mm, "end": v(21.34, -16.69) * mm});
            skLineSegment(sketch, "E44.19.2", {"start": v(21.34, -16.69) * mm, "end": v(21.07, -17.06) * mm});
            skLineSegment(sketch, "E44.19.3", {"start": v(20.76, -17.4) * mm, "end": v(21.07, -17.06) * mm});
            skArc(sketch, "E44.19.4", {"start": v(18.88, -17) * mm, "mid": v(19.8, -17.27) * mm, "end": v(20.76, -17.4) * mm});
            skLineSegment(sketch, "E44.19.5", {"start": v(18.88, -17) * mm, "end": v(17.62, -15.87) * mm});
            skLineSegment(sketch, "E44.20.0", {"start": v(23.2, -10.33) * mm, "end": v(21.66, -9.64) * mm});
            skArc(sketch, "E44.20.1", {"start": v(23.2, -10.33) * mm, "mid": v(23.83, -11.06) * mm, "end": v(24.34, -11.88) * mm});
            skLineSegment(sketch, "E44.20.2", {"start": v(24.34, -11.88) * mm, "end": v(24.15, -12.3) * mm});
            skLineSegment(sketch, "E44.20.3", {"start": v(23.92, -12.7) * mm, "end": v(24.15, -12.3) * mm});
            skArc(sketch, "E44.20.4", {"start": v(22, -12.7) * mm, "mid": v(22.96, -12.78) * mm, "end": v(23.92, -12.7) * mm});
            skLineSegment(sketch, "E44.20.5", {"start": v(22, -12.7) * mm, "end": v(20.53, -11.86) * mm});
            skLineSegment(sketch, "E44.21.0", {"start": v(24.84, -5.28) * mm, "end": v(23.2, -4.93) * mm});
            skArc(sketch, "E44.21.1", {"start": v(24.84, -5.28) * mm, "mid": v(25.61, -5.87) * mm, "end": v(26.28, -6.56) * mm});
            skLineSegment(sketch, "E44.21.2", {"start": v(26.28, -6.56) * mm, "end": v(26.19, -7.02) * mm});
            skLineSegment(sketch, "E44.21.3", {"start": v(26.04, -7.46) * mm, "end": v(26.19, -7.02) * mm});
            skArc(sketch, "E44.21.4", {"start": v(24.16, -7.85) * mm, "mid": v(25.11, -7.72) * mm, "end": v(26.04, -7.46) * mm});
            skLineSegment(sketch, "E44.21.5", {"start": v(24.16, -7.85) * mm, "end": v(22.55, -7.33) * mm});
            skLineSegment(sketch, "E44.22.0", {"start": v(25.4, 0) * mm, "end": v(23.71, 0) * mm});
            skArc(sketch, "E44.22.1", {"start": v(25.4, 0) * mm, "mid": v(26.27, -0.41) * mm, "end": v(27.07, -0.96) * mm});
            skLineSegment(sketch, "E44.22.2", {"start": v(27.07, -0.96) * mm, "end": v(27.07, -1.42) * mm});
            skLineSegment(sketch, "E44.22.3", {"start": v(27.02, -1.88) * mm, "end": v(27.07, -1.42) * mm});
            skArc(sketch, "E44.22.4", {"start": v(25.26, -2.66) * mm, "mid": v(26.17, -2.33) * mm, "end": v(27.02, -1.88) * mm});
            skLineSegment(sketch, "E44.22.5", {"start": v(25.26, -2.66) * mm, "end": v(23.58, -2.48) * mm});
            skLineSegment(sketch, "E44.23.0", {"start": v(24.84, 5.28) * mm, "end": v(23.2, 4.93) * mm});
            skArc(sketch, "E44.23.1", {"start": v(24.84, 5.28) * mm, "mid": v(25.78, 5.06) * mm, "end": v(26.68, 4.7) * mm});
            skLineSegment(sketch, "E44.23.2", {"start": v(26.68, 4.7) * mm, "end": v(26.78, 4.24) * mm});
            skLineSegment(sketch, "E44.23.3", {"start": v(26.82, 3.78) * mm, "end": v(26.78, 4.24) * mm});
            skArc(sketch, "E44.23.4", {"start": v(25.26, 2.66) * mm, "mid": v(26.09, 3.16) * mm, "end": v(26.82, 3.78) * mm});
            skLineSegment(sketch, "E44.23.5", {"start": v(25.26, 2.66) * mm, "end": v(23.58, 2.48) * mm});
            skLineSegment(sketch, "E44.24.0", {"start": v(23.2, 10.33) * mm, "end": v(21.66, 9.64) * mm});
            skArc(sketch, "E44.24.1", {"start": v(23.2, 10.33) * mm, "mid": v(24.17, 10.3) * mm, "end": v(25.12, 10.14) * mm});
            skLineSegment(sketch, "E44.24.2", {"start": v(25.12, 10.14) * mm, "end": v(25.3, 9.72) * mm});
            skLineSegment(sketch, "E44.24.3", {"start": v(25.45, 9.28) * mm, "end": v(25.3, 9.72) * mm});
            skArc(sketch, "E44.24.4", {"start": v(24.16, 7.85) * mm, "mid": v(24.86, 8.51) * mm, "end": v(25.45, 9.28) * mm});
            skLineSegment(sketch, "E44.24.5", {"start": v(24.16, 7.85) * mm, "end": v(22.55, 7.33) * mm});
            skLineSegment(sketch, "E44.25.0", {"start": v(20.55, 14.93) * mm, "end": v(19.18, 13.94) * mm});
            skArc(sketch, "E44.25.1", {"start": v(20.55, 14.93) * mm, "mid": v(21.5, 15.1) * mm, "end": v(22.46, 15.14) * mm});
            skLineSegment(sketch, "E44.25.2", {"start": v(22.46, 15.14) * mm, "end": v(22.74, 14.76) * mm});
            skLineSegment(sketch, "E44.25.3", {"start": v(22.97, 14.36) * mm, "end": v(22.74, 14.76) * mm});
            skArc(sketch, "E44.25.4", {"start": v(22, 12.7) * mm, "mid": v(22.55, 13.5) * mm, "end": v(22.97, 14.36) * mm});
            skLineSegment(sketch, "E44.25.5", {"start": v(22, 12.7) * mm, "end": v(20.53, 11.86) * mm});
            skLineSegment(sketch, "E44.26.0", {"start": v(17, 18.88) * mm, "end": v(15.87, 17.62) * mm});
            skArc(sketch, "E44.26.1", {"start": v(17, 18.88) * mm, "mid": v(17.89, 19.25) * mm, "end": v(18.83, 19.48) * mm});
            skLineSegment(sketch, "E44.26.2", {"start": v(18.83, 19.48) * mm, "end": v(19.17, 19.17) * mm});
            skLineSegment(sketch, "E44.26.3", {"start": v(19.48, 18.83) * mm, "end": v(19.17, 19.17) * mm});
            skArc(sketch, "E44.26.4", {"start": v(18.88, 17) * mm, "mid": v(19.25, 17.89) * mm, "end": v(19.48, 18.83) * mm});
            skLineSegment(sketch, "E44.26.5", {"start": v(18.88, 17) * mm, "end": v(17.62, 15.87) * mm});
            skLineSegment(sketch, "E44.27.0", {"start": v(12.7, 22) * mm, "end": v(11.86, 20.53) * mm});
            skArc(sketch, "E44.27.1", {"start": v(12.7, 22) * mm, "mid": v(13.5, 22.55) * mm, "end": v(14.36, 22.97) * mm});
            skLineSegment(sketch, "E44.27.2", {"start": v(14.36, 22.97) * mm, "end": v(14.76, 22.74) * mm});
            skLineSegment(sketch, "E44.27.3", {"start": v(15.14, 22.46) * mm, "end": v(14.76, 22.74) * mm});
            skArc(sketch, "E44.27.4", {"start": v(14.93, 20.55) * mm, "mid": v(15.1, 21.5) * mm, "end": v(15.14, 22.46) * mm});
            skLineSegment(sketch, "E44.27.5", {"start": v(14.93, 20.55) * mm, "end": v(13.94, 19.18) * mm});
            skLineSegment(sketch, "E44.28.0", {"start": v(7.85, 24.16) * mm, "end": v(7.33, 22.55) * mm});
            skArc(sketch, "E44.28.1", {"start": v(7.85, 24.16) * mm, "mid": v(8.51, 24.86) * mm, "end": v(9.28, 25.45) * mm});
            skLineSegment(sketch, "E44.28.2", {"start": v(9.28, 25.45) * mm, "end": v(9.72, 25.3) * mm});
            skLineSegment(sketch, "E44.28.3", {"start": v(10.14, 25.12) * mm, "end": v(9.72, 25.3) * mm});
            skArc(sketch, "E44.28.4", {"start": v(10.33, 23.2) * mm, "mid": v(10.3, 24.17) * mm, "end": v(10.14, 25.12) * mm});
            skLineSegment(sketch, "E44.28.5", {"start": v(10.33, 23.2) * mm, "end": v(9.64, 21.66) * mm});
            skLineSegment(sketch, "E44.29.0", {"start": v(2.66, 25.26) * mm, "end": v(2.48, 23.58) * mm});
            skArc(sketch, "E44.29.1", {"start": v(2.66, 25.26) * mm, "mid": v(3.16, 26.09) * mm, "end": v(3.78, 26.82) * mm});
            skLineSegment(sketch, "E44.29.2", {"start": v(3.78, 26.82) * mm, "end": v(4.24, 26.78) * mm});
            skLineSegment(sketch, "E44.29.3", {"start": v(4.7, 26.68) * mm, "end": v(4.24, 26.78) * mm});
            skArc(sketch, "E44.29.4", {"start": v(5.28, 24.84) * mm, "mid": v(5.06, 25.78) * mm, "end": v(4.7, 26.68) * mm});
            skLineSegment(sketch, "E44.29.5", {"start": v(5.28, 24.84) * mm, "end": v(4.93, 23.2) * mm});
            skArc(sketch, "E45.trimOffspring", {"start": v(-7.33, 22.55) * mm, "mid": v(-8.5, 22.14) * mm, "end": v(-9.64, 21.66) * mm});
            skArc(sketch, "E46.trimOffspring", {"start": v(2.48, 23.58) * mm, "mid": v(1.24, 23.68) * mm, "end": v(0, 23.71) * mm});
            skArc(sketch, "E47.trimOffspring", {"start": v(-11.86, 20.53) * mm, "mid": v(-12.91, 19.89) * mm, "end": v(-13.94, 19.18) * mm});
            skArc(sketch, "E48.trimOffspring", {"start": v(7.33, 22.55) * mm, "mid": v(6.14, 22.9) * mm, "end": v(4.93, 23.2) * mm});
            skArc(sketch, "E49.trimOffspring", {"start": v(-15.87, 17.62) * mm, "mid": v(-16.77, 16.77) * mm, "end": v(-17.62, 15.87) * mm});
            skArc(sketch, "E50.trimOffspring", {"start": v(11.86, 20.53) * mm, "mid": v(10.76, 21.13) * mm, "end": v(9.64, 21.66) * mm});
            skArc(sketch, "E51.trimOffspring", {"start": v(15.87, 17.62) * mm, "mid": v(14.92, 18.43) * mm, "end": v(13.94, 19.18) * mm});
            skArc(sketch, "E52.trimOffspring", {"start": v(-19.18, 13.94) * mm, "mid": v(-19.89, 12.91) * mm, "end": v(-20.53, 11.86) * mm});
            skArc(sketch, "E53.trimOffspring", {"start": v(-21.66, 9.64) * mm, "mid": v(-22.14, 8.5) * mm, "end": v(-22.55, 7.33) * mm});
            skArc(sketch, "E54.trimOffspring", {"start": v(-23.2, 4.93) * mm, "mid": v(-23.42, 3.7) * mm, "end": v(-23.58, 2.48) * mm});
            skArc(sketch, "E55.trimOffspring", {"start": v(21.66, 9.64) * mm, "mid": v(21.13, 10.76) * mm, "end": v(20.53, 11.86) * mm});
            skArc(sketch, "E56.trimOffspring", {"start": v(19.18, 13.94) * mm, "mid": v(18.43, 14.92) * mm, "end": v(17.62, 15.87) * mm});
            skArc(sketch, "E57.trimOffspring", {"start": v(-2.48, -23.58) * mm, "mid": v(-1.24, -23.68) * mm, "end": v(0, -23.71) * mm});
            skArc(sketch, "E58.trimOffspring", {"start": v(-7.33, -22.55) * mm, "mid": v(-6.14, -22.9) * mm, "end": v(-4.93, -23.2) * mm});
            skArc(sketch, "E59.trimOffspring", {"start": v(-11.86, -20.53) * mm, "mid": v(-10.76, -21.13) * mm, "end": v(-9.64, -21.66) * mm});
            skArc(sketch, "E60.trimOffspring", {"start": v(-15.87, -17.62) * mm, "mid": v(-14.92, -18.43) * mm, "end": v(-13.94, -19.18) * mm});
            skArc(sketch, "E61.trimOffspring", {"start": v(-19.18, -13.94) * mm, "mid": v(-18.43, -14.92) * mm, "end": v(-17.62, -15.87) * mm});
            skArc(sketch, "E62.trimOffspring", {"start": v(-21.66, -9.64) * mm, "mid": v(-21.13, -10.76) * mm, "end": v(-20.53, -11.86) * mm});
            skArc(sketch, "E63.trimOffspring", {"start": v(-23.2, -4.93) * mm, "mid": v(-22.9, -6.14) * mm, "end": v(-22.55, -7.33) * mm});
            skArc(sketch, "E64.trimOffspring", {"start": v(-23.71, 0) * mm, "mid": v(-23.68, -1.24) * mm, "end": v(-23.58, -2.48) * mm});
            skArc(sketch, "E65.trimOffspring", {"start": v(23.2, 4.93) * mm, "mid": v(22.9, 6.14) * mm, "end": v(22.55, 7.33) * mm});
            skArc(sketch, "E66.trimOffspring", {"start": v(23.71, 0) * mm, "mid": v(23.68, 1.24) * mm, "end": v(23.58, 2.48) * mm});
            skArc(sketch, "E67.trimOffspring", {"start": v(23.2, -4.93) * mm, "mid": v(23.42, -3.7) * mm, "end": v(23.58, -2.48) * mm});
            skArc(sketch, "E68.trimOffspring", {"start": v(21.66, -9.64) * mm, "mid": v(22.14, -8.5) * mm, "end": v(22.55, -7.33) * mm});
            skArc(sketch, "E69.trimOffspring", {"start": v(19.18, -13.94) * mm, "mid": v(19.89, -12.91) * mm, "end": v(20.53, -11.86) * mm});
            skArc(sketch, "E70.trimOffspring", {"start": v(15.87, -17.62) * mm, "mid": v(16.77, -16.77) * mm, "end": v(17.62, -15.87) * mm});
            skArc(sketch, "E71.trimOffspring", {"start": v(11.86, -20.53) * mm, "mid": v(12.91, -19.89) * mm, "end": v(13.94, -19.18) * mm});
            skArc(sketch, "E72.trimOffspring", {"start": v(7.33, -22.55) * mm, "mid": v(8.5, -22.14) * mm, "end": v(9.64, -21.66) * mm});
            skArc(sketch, "E73.trimOffspring", {"start": v(2.48, -23.58) * mm, "mid": v(3.7, -23.42) * mm, "end": v(4.93, -23.2) * mm});
            skSolve(sketch);
        }
        {
            var Q0;
            Q0=makeQuery(id+"F0.imprint","IMPRINT",FACE,{"disambiguationData":[TD([[makeQuery(id+"F0.imprint","IMPRINT",EDGE,{"derivedFrom":sQuery(id+"F0.wireOp",EDGE,"E0")}),1.0]])]});
            var Q1;
            Q1=makeQuery(id+"F2.imprint","IMPRINT",FACE,{"disambiguationData":[TD([[makeQuery(id+"F2.imprint","IMPRINT",EDGE,{"derivedFrom":sQuery(id+"F2.wireOp",EDGE,"E37")}),1.0]])]});
            var Q2;
            Q2=sQuery(id+"F2.wireOp",VERTEX,"E41.MirrorCS.end");
            var Q3;
            Q3=sQuery(id+"F0.wireOp",VERTEX,"E7.29.3.end");
            loft(context, id + "F3", {"sheetProfilesArray" : [{ "sheetProfileEntities" : qUnion([Q0]) }, { "sheetProfileEntities" : qUnion([Q1]) }], "matchConnections" : true, "connections" : [{ "connectionEntities" : qUnion([Q2, Q3]), "connectionEdgeQueries" : qUnion([]), "connectionEdgeParameters" : [] }]});
        }
        {
            var Q0;
            Q0=makeQuery(id+"F3.opLoft","CAP_FACE",FACE,{"disambiguationData":[OSD([makeQuery(id+"F2.imprint","IMPRINT",FACE,{"disambiguationData":[TD([[makeQuery(id+"F2.imprint","IMPRINT",EDGE,{"derivedFrom":sQuery(id+"F2.wireOp",EDGE,"E37")}),1.0]])]})])],"isStart":true});
            var sketch = newSketch(context, id + "F4", { "sketchPlane" : qUnion([Q0])});
            skCircle(sketch, "E74", {"center": v(0, 0) * mm, "radius": 6.35 * mm});
            skSolve(sketch);
        }
        {
            var Q0;
            Q0=makeQuery(id+"F4.imprint","IMPRINT",FACE,{"disambiguationData":[TD([[makeQuery(id+"F4.imprint","IMPRINT",EDGE,{"derivedFrom":sQuery(id+"F4.wireOp",EDGE,"E74")}),1.0]])]});
            extrude(context, id + "F5", {"entities" : qUnion([Q0]), "operationType" : NewBodyOperationType.REMOVE, "endBound" : BoundingType.THROUGH_ALL, "oppositeDirection" : true, "depth" : 25.4 * mm});
        }
    });
